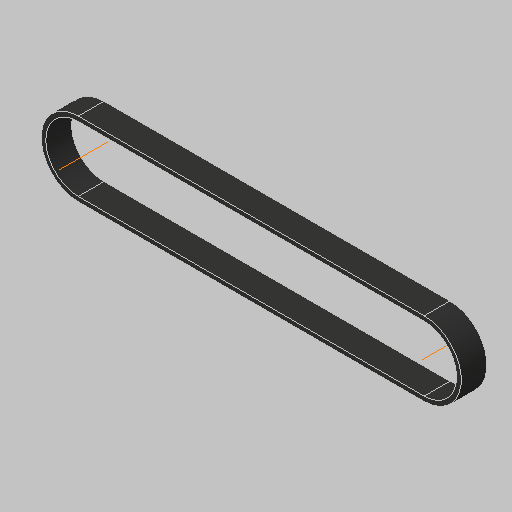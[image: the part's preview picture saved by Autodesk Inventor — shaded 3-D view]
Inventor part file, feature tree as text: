
AUTODESK INVENTOR PART (.ipt)
format: ipt  version: 2023.5 (Build 275446000, 446)  size: 163,328 bytes
history: native  units: in
note: dims shown in document units (in); Inventor stores cm internally (conversion verified against a paired STEP export)
features: sketch x3, extrude x1, other x1, projected_geometry x1
ambient origin geometry x8: Origin, YZ Plane, XZ Plane, XY Plane, X Axis, Y Axis, Z Axis, Center Point
bodies: Body1 (feature_tree)
feature tree (6):
  sketch  "Sketch2"  dims[d0=0.9023in d1=0.9023in]
  extrude  "Extrusion2"  Depth=0.9023in
  sketch  "Sketch5"  dims[d3=1.4174in d5=4.4881in d9=0.0787in d10=0.0598in d11=0.0299in d12=0.0219in d13=0.0219in d14=0.0059in d15=0.0059in d20=0.3346in d21=0.0in d22=0.0787in d23=0.0598in d24=0.0299in d25=0.0219in d26=0.0219in d27=0.0059in d28=0.0059in d29=0.0299in d30=0.0394in d31=0.0787in d32=0.0232in d34=0.0219in d35=0.0in d36=0.0in d37=0.0059in d38=0.0022in d39=0.0022in d40=0.0in d41=0.0in d42=0.0081in d43=0.0081in d44=0.0299in]
  other  "Work Axis1"
  sketch  "Sketch4"  dims[d2=1.4174in]
  projected_geometry  "Projected Loop1"
